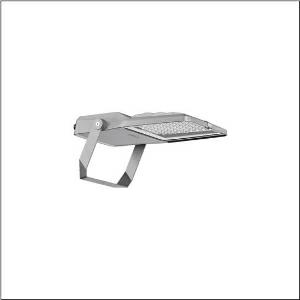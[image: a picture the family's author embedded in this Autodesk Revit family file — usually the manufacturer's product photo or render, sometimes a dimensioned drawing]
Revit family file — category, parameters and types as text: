
# Revit family: floodlight_fl_21_iq_mini___pl43_5xa7772d5a1a_690f
name_source: partatom
category: Lighting Fixtures
units: mm (PartAtom-declared; Revit-internal decimal feet)

## family parameters
Cut with Voids When Loaded = No
Host = Face
Light Source = No
Part Type = Normal
Room Calculation Point = No
Round Connector Dimension = Use Diameter
Shared = No

## types (1)
- --- (1 x LED, 17070 lm, 143 W, 4000K)
    Apparent Load = 143 VA
    CIE Flux Codes = 27 78 99 100 100
    Color Rendering = 80
    Color Temperature = 4000K
    Default Elevation = 1800 mm
    Description = Floodlight FL 21 iQ mini, floodlight, primary light control with lens, of PMMA, primary optical cover: protective disc, of toughened safety glass, transparent, light distribution: PL43, light emission: direct distribution, installation type: surface-mounted, lamps: LED, High Power LED, rated values: 17.070lm | 143W | 119,4lm/W (begin service life); end service life: 17.070lm | 151,6W; at 50% lumin. flux: 8.535lm | 60,6W | 140,8lm/W, colour temperature: 4000K, colour rendering: CRI > 80, light colour: 840, light setting 1 begin service life: 100% | 17.070lm | 143W | 119,4lm/W | 4.000K, light setting 1 end service life: 151,6W, further light settings possible, control: Street-Remote, Auto-Match, Temp-Guard, Night-Set, Smart-Wire, Desk-Remote (wireless, voltage-free reading and setting of iQ features in the workshop via application-optimized NFC function/RFID function), optimised constant luminous flux control (CLO 2.0), pre-setting: linear dimming characteristic, with terminal, 6-pole, mains connection: 220..240V, AC, 50/60Hz, luminaire housing, of diecast aluminium, powder-coated, SITECO metallic grey (DB 702S), corrosivity category C5 mid according to DIN EN ISO 12944suitable for swimming poolschlorine-resistant, sealing non-destructively replaceable, mounting bracket, of steel, galvanised, powder-coated, SITECO metallic grey (DB 702S), protection rating (complete): IP66, insulation class (complete): insulation class II (safety insulation), certification: CE, ENEC, VDE, protection symbol: D, impact resistance: IK08, permissible operating ambient temperature: -40..+40°C, permissible operating ambient temperature for outdoor applications: -40..+50°C, standard: DIN EN 12944, LABS conformity tested according to VDMA 24364:2018-05, packaging unit: 1 piece

Light Distribution: PL43
    Height = 70 mm
    Lamp = 1 x LED
    Lamp Light Flux = 17070 lm
    Lamp Power = 143 W
    Lamp count = 1
    Length = 485 mm
    Luminous efficacy = 119 lm/W
    Manufacturer = Siteco
    ModVariant = No
    Model = 5XA7772D5A1A
    Number of Poles = 1
    OnlyDefault = Yes
    Power Factor = 1
    Product Name = Floodlight FL 21 iQ mini | PL43
    Product group = floodlight | pylon annexe
    ProductGroupID = 6201
    Protection Class = Protection class II
    Protection Degree = IP 66
    RLX_Detail_Level = 1
    RLX_Emergency_Light_Flux = 0 lm
    RLX_Emergency_Type = 0
    RLX_Emergency_Type_DB = No
    RlxData = <blob elided: 96689 chars, md5=b3b2c126>
    Socket = socket
    Standby Power = 0 W
    System Light Flux = 17070 lm
    System Power = 143 W
    Type Comments = factory setting: luminous flux: 100 % | dim-lin: 254 | 730 mA
    Type Image = l_1006845.jpg
    URL = http://relux.com
    VarID = @adj_160897
    Voltage = 0 V
    Weight = 0.00 kg
    Width = 337 mm

## geometry (parser evidence)
native form markers: Blend x4, Sweep x11
no freeform markers — native parametric forms only
